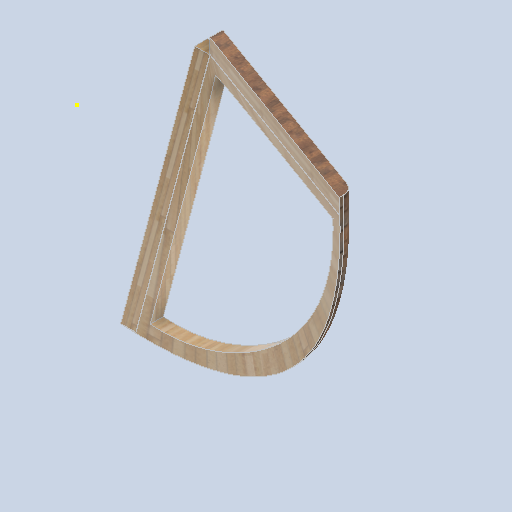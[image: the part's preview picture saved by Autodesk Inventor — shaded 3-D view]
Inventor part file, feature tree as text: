
AUTODESK INVENTOR PART (.ipt)
format: ipt  version: 2024.2 (Build 282272000, 272)  size: 296,448 bytes
history: native  units: in
note: dims shown in document units (in); Inventor stores cm internally (conversion verified against a paired STEP export)
features: sketch x12, plane x8, other x3
ambient origin geometry x8: Origin, YZ Plane, XZ Plane, XY Plane, X Axis, Y Axis, Z Axis, Center Point
bodies: Solid1 (feature_tree)
feature tree (23):
  other  "side_curve_corner_frame.ipt"
  other  "Solid1::side_curve_corner_frame.ipt"
  other  "TaggingFeature1"
  sketch  "Sketch1"  dims[d0=0.3937in]
  sketch  "Sketch2"
  sketch  "Sketch3"
  sketch  "Sketch4"
  sketch  "Sketch5"
  sketch  "Sketch6"
  sketch  "Sketch7"
  sketch  "Sketch8"
  sketch  "Sketch10"
  sketch  "Sketch11"
  sketch  "Sketch12"
  sketch  "Sketch14"
  plane  "Work Plane1"
  plane  "Work Plane2"
  plane  "Work Plane3"
  plane  "Work Plane4"
  plane  "Work Plane5"
  plane  "Work Plane6"
  plane  "Work Plane7"
  plane  "Work Plane8"
